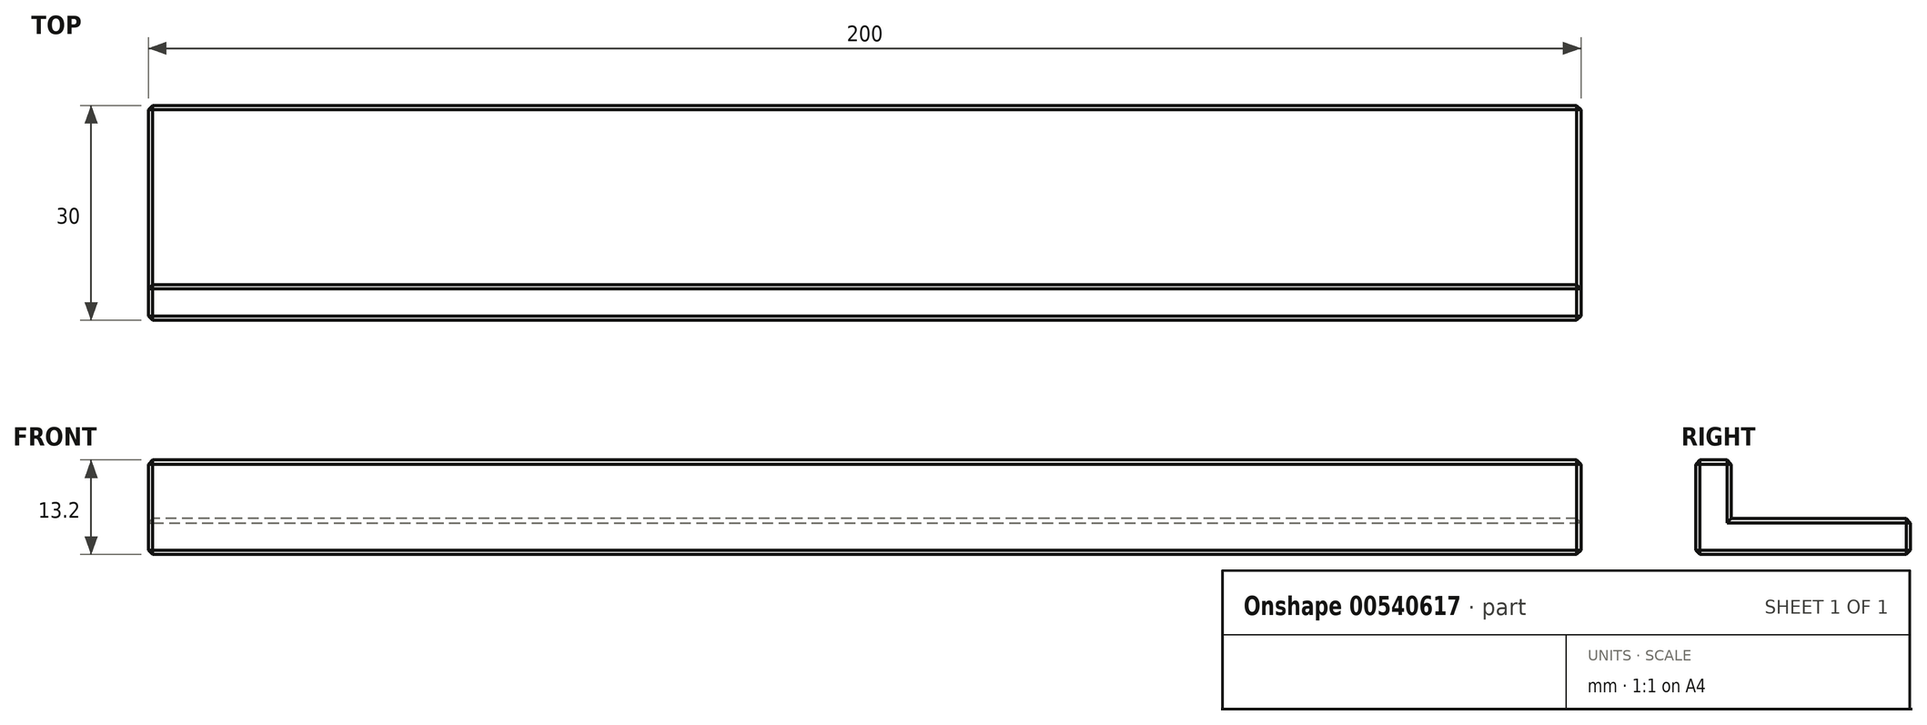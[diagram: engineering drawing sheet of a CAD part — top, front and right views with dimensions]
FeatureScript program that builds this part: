
annotation { "Feature Type Name" : "Feature", "Feature Type Description" : "" }
export const myFeature = defineFeature(function(context is Context, id is Id, definition is map)
    precondition{}
    {
        {
            var Q0;
            Q0=qCreatedBy(makeId("Top.planeOp"),FACE);
            var sketch = newSketch(context, id + "F0", { "sketchPlane" : qUnion([Q0])});
            skLineSegment(sketch, "E0.bottom", {"start": v(0, 0) * mm, "end": v(200, 0) * mm});
            skLineSegment(sketch, "E0.top", {"start": v(0, 25) * mm, "end": v(200, 25) * mm});
            skLineSegment(sketch, "E0.left", {"start": v(0, 0) * mm, "end": v(0, 25) * mm});
            skLineSegment(sketch, "E0.right", {"start": v(200, 0) * mm, "end": v(200, 25) * mm});
            skLineSegment(sketch, "E1.0", {"start": v(0, -5) * mm, "end": v(200, -5) * mm, "construction": true});
            skLineSegment(sketch, "E2.top", {"start": v(0, -5) * mm, "end": v(200, -5) * mm});
            skLineSegment(sketch, "E2.left", {"start": v(0, 0) * mm, "end": v(0, -5) * mm});
            skLineSegment(sketch, "E2.right", {"start": v(200, 0) * mm, "end": v(200, -5) * mm});
            skSolve(sketch);
        }
        {
            var Q0;
            Q0 = qSketchRegion(id + "F0", true);
            extrude(context, id + "F1", {"entities" : qUnion([Q0]), "depth" : 5 * mm, "offsetDistance" : 25 * mm});
        }
        {
            var Q0;
            Q0=makeQuery(id+"F0.imprint","IMPRINT",FACE,{"disambiguationData":[TD([[makeQuery(id+"F0.imprint","IMPRINT",EDGE,{"derivedFrom":sQuery(id+"F0.wireOp",EDGE,"E0.bottom")}),-1.0]])]});
            extrude(context, id + "F2", {"entities" : qUnion([Q0]), "operationType" : NewBodyOperationType.ADD, "depth" : (5 + 6 + 2.2) * mm, "offsetDistance" : 25 * mm});
        }
        {
            var Q0;
            Q0=makeQuery(id+"F1.opExtrude","CAP_EDGE",EDGE,{"disambiguationData":[OSD([sQuery(id+"F0.wireOp",EDGE,"E0.top")])],"isStart":false});
            var Q1;
            Q1=makeQuery(id+"F1.opExtrude","CAP_EDGE",EDGE,{"disambiguationData":[OSD([sQuery(id+"F0.wireOp",EDGE,"E0.right"),sQuery(id+"F0.wireOp",EDGE,"E2.right")])],"isStart":false});
            var Q2;
            Q2=makeQuery(id+"F1.opExtrude","SWEPT_EDGE",EDGE,{"disambiguationData":[OSD([sQuery(id+"F0.wireOp",EDGE,"E0.top"),sQuery(id+"F0.wireOp",EDGE,"E0.right")])]});
            var Q3;
            Q3=makeQuery(id+"F1.opExtrude","CAP_EDGE",EDGE,{"disambiguationData":[OSD([sQuery(id+"F0.wireOp",EDGE,"E0.right"),sQuery(id+"F0.wireOp",EDGE,"E2.right")])],"isStart":true});
            var Q4;
            {var subQ0=sQuery(id+"F0.wireOp",EDGE,"E2.right");var subQ1=sQuery(id+"F0.wireOp",EDGE,"E2.top");Q4=makeQuery(id+"F2.boolean.opBoolean","MERGE",EDGE,{"derivedFrom":[makeQuery(id+"F1.opExtrude","SWEPT_EDGE",EDGE,{"disambiguationData":[OSD([subQ1,subQ0])]}),makeQuery(id+"F2.opExtrude","SWEPT_EDGE",EDGE,{"disambiguationData":[OSD([subQ1,subQ0])]})]});}
            var Q5;
            {var subQ0=sQuery(id+"F0.wireOp",EDGE,"E2.right");Q5=makeQuery(id+"F2.boolean.opBoolean","MERGE",FACE,{"derivedFrom":[makeQuery(id+"F1.opExtrude","SWEPT_FACE",FACE,{"disambiguationData":[OSD([sQuery(id+"F0.wireOp",EDGE,"E0.right"),subQ0])]}),makeQuery(id+"F2.opExtrude","SWEPT_FACE",FACE,{"disambiguationData":[OSD([subQ0])]})]});}
            var Q6;
            Q6=makeQuery(id+"F1.opExtrude","SWEPT_FACE",FACE,{"disambiguationData":[OSD([sQuery(id+"F0.wireOp",EDGE,"E0.top")])]});
            var Q7;
            {var subQ0=sQuery(id+"F0.wireOp",EDGE,"E2.left");Q7=makeQuery(id+"F2.boolean.opBoolean","MERGE",FACE,{"derivedFrom":[makeQuery(id+"F1.opExtrude","SWEPT_FACE",FACE,{"disambiguationData":[OSD([sQuery(id+"F0.wireOp",EDGE,"E0.left"),subQ0])]}),makeQuery(id+"F2.opExtrude","SWEPT_FACE",FACE,{"disambiguationData":[OSD([subQ0])]})]});}
            var Q8;
            Q8=makeQuery(id+"F2.opExtrude","CAP_FACE",FACE,{"disambiguationData":[OSD([sQuery(id+"F0.wireOp",EDGE,"E0.bottom"),sQuery(id+"F0.wireOp",EDGE,"E2.top"),sQuery(id+"F0.wireOp",EDGE,"E2.left"),sQuery(id+"F0.wireOp",EDGE,"E2.right")])],"isStart":false});
            var Q9;
            {var subQ0=sQuery(id+"F0.wireOp",EDGE,"E2.top");Q9=makeQuery(id+"F2.boolean.opBoolean","MERGE",FACE,{"derivedFrom":[makeQuery(id+"F1.opExtrude","SWEPT_FACE",FACE,{"disambiguationData":[OSD([subQ0])]}),makeQuery(id+"F2.opExtrude","SWEPT_FACE",FACE,{"disambiguationData":[OSD([subQ0])]})]});}
            chamfer(context, id + "F3", {"entities" : qUnion([Q0, Q1, Q2, Q3, Q4, Q5, Q6, Q7, Q8, Q9]), "width" : 0.6 * mm, "tangentPropagation" : true});
        }
    });
